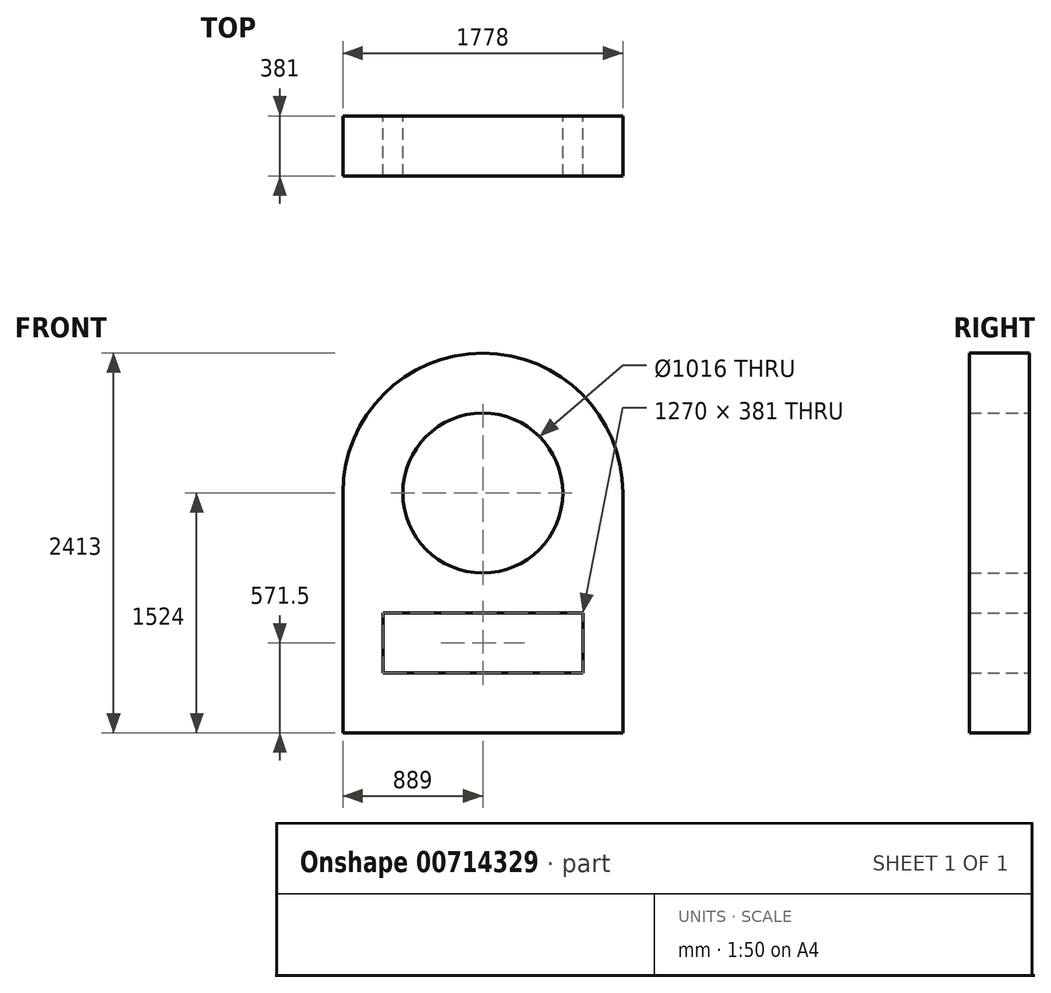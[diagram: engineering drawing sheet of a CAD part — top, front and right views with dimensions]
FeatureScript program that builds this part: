
annotation { "Feature Type Name" : "Feature", "Feature Type Description" : "" }
export const myFeature = defineFeature(function(context is Context, id is Id, definition is map)
    precondition{}
    {
        {
            var Q0;
            Q0=qCreatedBy(makeId("Front.planeOp"),FACE);
            var sketch = newSketch(context, id + "F0", { "sketchPlane" : qUnion([Q0])});
            skLineSegment(sketch, "E0", {"start": v(0, 0) * mm, "end": v(1778, 0) * mm});
            skLineSegment(sketch, "E1", {"start": v(1778, 0) * mm, "end": v(1778, 1524) * mm});
            skLineSegment(sketch, "E2", {"start": v(0, 0) * mm, "end": v(0, 1524) * mm});
            skLineSegment(sketch, "E3", {"start": v(254, 381) * mm, "end": v(254, 762) * mm});
            skLineSegment(sketch, "E4", {"start": v(254, 762) * mm, "end": v(1524, 762) * mm});
            skLineSegment(sketch, "E5", {"start": v(1524, 762) * mm, "end": v(1524, 381) * mm});
            skLineSegment(sketch, "E6", {"start": v(1524, 381) * mm, "end": v(254, 381) * mm});
            skArc(sketch, "E7", {"start": v(1778, 1524) * mm, "mid": v(889, 2413) * mm, "end": v(0, 1524) * mm});
            skCircle(sketch, "E8", {"center": v(889, 1524) * mm, "radius": 508 * mm});
            skSolve(sketch);
        }
        {
            var Q0;
            Q0 = qSketchRegion(id + "F0", true);
            extrude(context, id + "F1", {"entities" : qUnion([Q0]), "depth" : 381 * mm, "offsetDistance" : 25.4 * mm});
        }
    });
